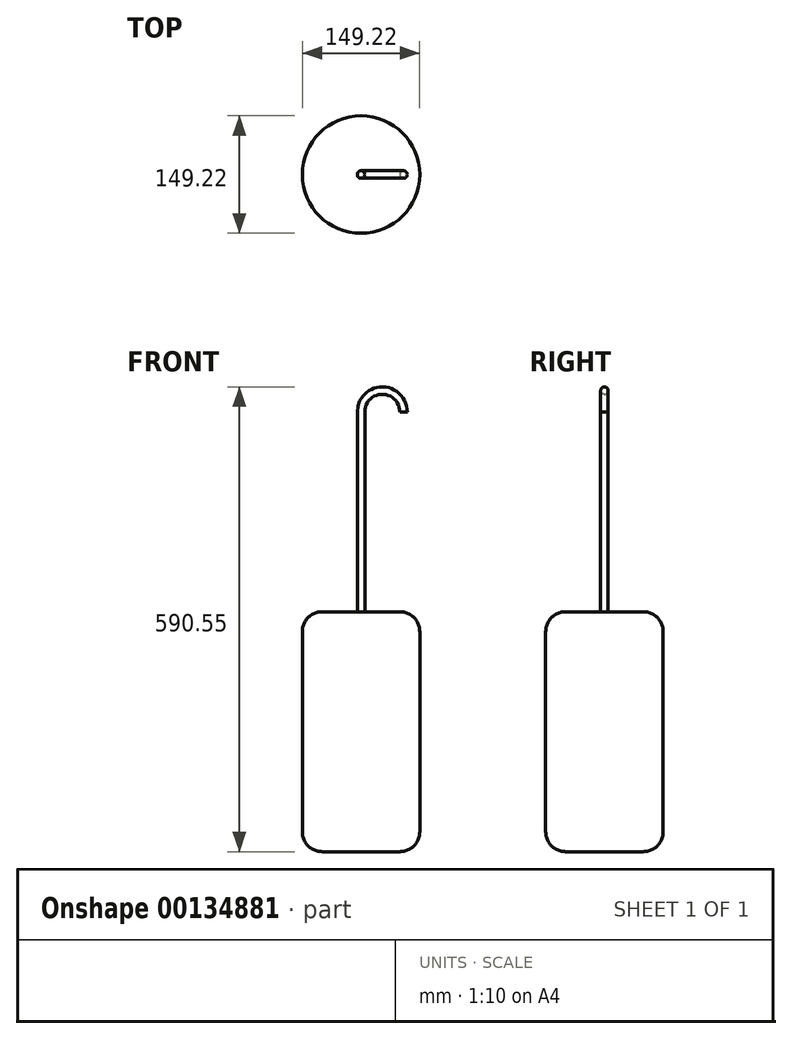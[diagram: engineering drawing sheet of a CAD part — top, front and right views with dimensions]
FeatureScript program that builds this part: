
annotation { "Feature Type Name" : "Feature", "Feature Type Description" : "" }
export const myFeature = defineFeature(function(context is Context, id is Id, definition is map)
    precondition{}
    {
        {
            var Q0;
            Q0=qCreatedBy(makeId("Front.planeOp"),FACE);
            var sketch = newSketch(context, id + "F0", { "sketchPlane" : qUnion([Q0])});
            skLineSegment(sketch, "E0.bottom", {"start": v(-49.21, 228.6) * mm, "end": v(0, 228.6) * mm});
            skLineSegment(sketch, "E0.top", {"start": v(-49.21, -76.2) * mm, "end": v(0, -76.2) * mm});
            skLineSegment(sketch, "E0.left", {"start": v(-74.61, 203.2) * mm, "end": v(-74.61, -50.8) * mm});
            skPoint(sketch, "E0.middle", {"position": v(0, 0) * mm});
            skPoint(sketch, "E1.visualSharp", {"position": v(-74.61, 228.6) * mm});
            skArc(sketch, "E1.filletArc", {"start": v(-49.21, 228.6) * mm, "mid": v(-67.17, 221.16) * mm, "end": v(-74.61, 203.2) * mm});
            skPoint(sketch, "E2.visualSharp", {"position": v(-74.61, -76.2) * mm});
            skArc(sketch, "E2.filletArc", {"start": v(-74.61, -50.8) * mm, "mid": v(-67.17, -68.76) * mm, "end": v(-49.21, -76.2) * mm});
            skLineSegment(sketch, "E3", {"start": v(0, 228.6) * mm, "end": v(0, 482.6) * mm});
            skPoint(sketch, "E3.endSnap0", {"position": v(0, 228.6) * mm});
            skArc(sketch, "E4", {"start": v(53.98, 482.6) * mm, "mid": v(26.99, 509.59) * mm, "end": v(0, 482.6) * mm});
            skLineSegment(sketch, "E5", {"start": v(0, 228.6) * mm, "end": v(0, -76.2) * mm});
            skSolve(sketch);
        }
        {
            var Q0;
            Q0=makeQuery(id+"F0.imprint","IMPRINT",FACE,{"disambiguationData":[TD([[makeQuery(id+"F0.imprint","IMPRINT",EDGE,{"derivedFrom":sQuery(id+"F0.wireOp",EDGE,"E0.bottom")}),-1.0]])]});
            var Q1;
            Q1=sQuery(id+"F0.wireOp",EDGE,"E5");
            revolve(context, id + "F1", {"entities" : qUnion([Q0]), "axis" : qUnion([Q1]), "revolveType" : RevolveType.FULL});
        }
        {
            var Q0;
            Q0=makeQuery(id+"F1.opRevolve","SWEPT_FACE",FACE,{"disambiguationData":[OSD([sQuery(id+"F0.wireOp",EDGE,"E0.bottom")])]});
            var sketch = newSketch(context, id + "F2", { "sketchPlane" : qUnion([Q0])});
            skCircle(sketch, "E6", {"center": v(0, 0) * mm, "radius": 4.76 * mm});
            skSolve(sketch);
        }
        {
            var Q0;
            Q0=makeQuery(id+"F2.imprint","IMPRINT",FACE,{"disambiguationData":[TD([[makeQuery(id+"F2.imprint","IMPRINT",EDGE,{"derivedFrom":sQuery(id+"F2.wireOp",EDGE,"E6")}),1.0]])]});
            var Q1;
            Q1=sQuery(id+"F2.wireOp",EDGE,"E6");
            var Q2;
            Q2=sQuery(id+"F0.wireOp",EDGE,"E3");
            var Q3;
            Q3=sQuery(id+"F0.wireOp",EDGE,"E4");
            var Q4;
            Q4=sQuery(id+"F0.wireOp",EDGE,"WNapF5jK-r5oZ-O1Ue-4YwV-uUyhPFQVmQXx");
            sweep(context, id + "F3", {"operationType" : NewBodyOperationType.ADD, "profiles" : qUnion([Q0]), "surfaceProfiles" : qUnion([Q1]), "path" : qUnion([Q2, Q3, Q4])});
        }
    });
